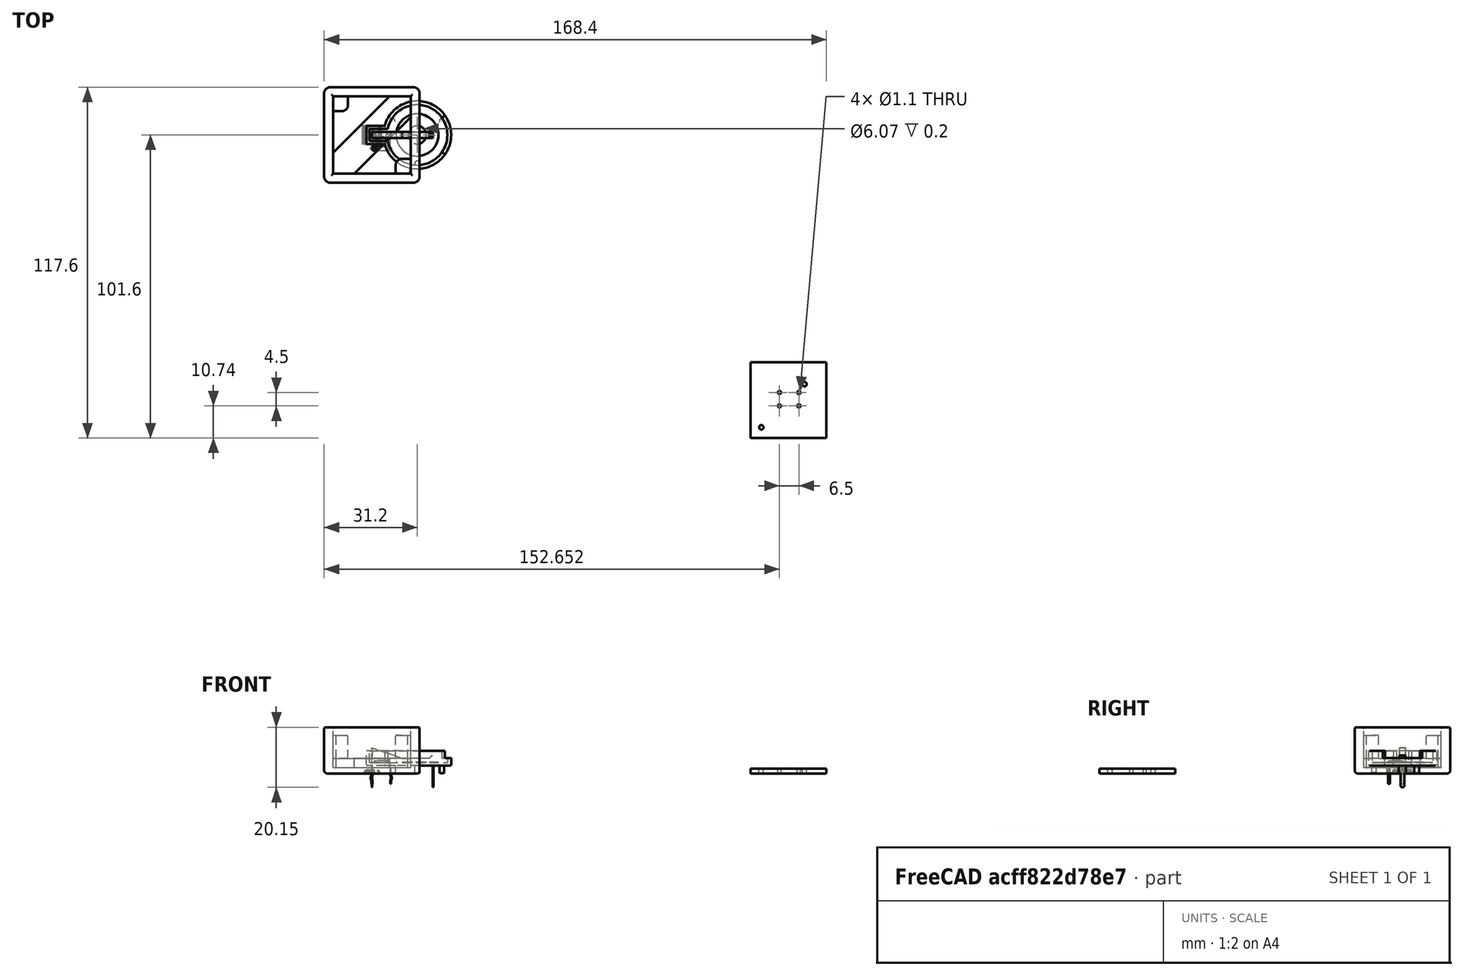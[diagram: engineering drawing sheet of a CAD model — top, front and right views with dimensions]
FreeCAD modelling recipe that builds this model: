
FCSTD DOCUMENT  (FreeCAD 0.18R16131 (Git))
Label: BoxSup
License: All rights reserved
LicenseURL: http://en.wikipedia.org/wiki/All_rights_reserved
objects: Part::Feature×30, App::Part×30, Part::Box×7, Part::Fillet×6, Part::MultiFuse×2, Part::Cut×2
note: 47 computed .brp shape members not serialized (recipe doc carries the construction recipe); baked Part::Feature solids carry a one-line shape summary decoded from their .brp

FEATURE [Part::Box] Box  label="MainInside"
  AttacherType = Attacher::AttachEngine3D
  Height = 20
  Length = 26
  Placement = pos=(-13,-13,-10) rot=(0,0,1;0rad)
  Width = 26
FEATURE [Part::Feature] Part__Feature  label="SOLID"
  shape: bbox 2 x 1.25 x 1.1 mm, 50 faces (baked)
FEATURE [App::Part] LED_0805_2012Metric
  Group = -> [Part__Feature]
  License = CC BY 3.0
  LicenseURL = http://creativecommons.org/licenses/by/3.0/
  Origin = -> Origin
  Placement = pos=(144.272,-79.248,1.65) rot=(0,0,-1;1.5708rad)
FEATURE [Part::Feature] Part__Feature001  label="SOLID001"
  shape: bbox 7.174 x 6 x 7.8 mm, 105 faces (baked)
FEATURE [App::Part] SW_PUSH_6mm
  Group = -> [Part__Feature001]
  License = CC BY 3.0
  LicenseURL = http://creativecommons.org/licenses/by/3.0/
  Origin = -> Origin001
  Placement = pos=(136.652,-86.36,1.65) rot=(0,0,1;0rad)
FEATURE [Part::Feature] Part__Feature002  label="SOLID002"
  shape: bbox 1.6 x 0.8 x 0.45 mm, 26 faces (baked)
FEATURE [App::Part] R_0603_1608Metric
  Group = -> [Part__Feature002]
  License = CC BY 3.0
  LicenseURL = http://creativecommons.org/licenses/by/3.0/
  Origin = -> Origin002
  Placement = pos=(147.701,-98.679,1.65) rot=(0,0,1;0rad)
FEATURE [Part::Feature] Part__Feature003  label="SOLID003"
  shape: bbox 1.6 x 0.8 x 0.45 mm, 26 faces (baked)
FEATURE [App::Part] R_0603_1608Metric001
  Group = -> [Part__Feature003]
  License = CC BY 3.0
  LicenseURL = http://creativecommons.org/licenses/by/3.0/
  Origin = -> Origin003
  Placement = pos=(145.411,-99.187,1.65) rot=(0,0,1;1.5708rad)
FEATURE [Part::Feature] Part__Feature004  label="SOLID004"
  shape: bbox 6.4 x 6.5 x 1.2 mm, 336 faces (baked)
FEATURE [App::Part] TSSOP_20_4_4x6_5mm_P0_65mm
  Group = -> [Part__Feature004]
  License = CC BY 3.0
  LicenseURL = http://creativecommons.org/licenses/by/3.0/
  Origin = -> Origin004
  Placement = pos=(148.336,-93.81,1.65) rot=(0,0,1;1.5708rad)
FEATURE [Part::Feature] Part__Feature005  label="SOLID005"
  shape: bbox 2 x 1.25 x 1.1 mm, 50 faces (baked)
FEATURE [App::Part] LED_0805_2012Metric001
  Group = -> [Part__Feature005]
  License = CC BY 3.0
  LicenseURL = http://creativecommons.org/licenses/by/3.0/
  Origin = -> Origin005
  Placement = pos=(130.556,-79.248,1.65) rot=(0,0,-1;1.5708rad)
FEATURE [Part::Feature] Part__Feature006  label="SOLID006"
  shape: bbox 2 x 1.25 x 1.1 mm, 50 faces (baked)
FEATURE [App::Part] LED_0805_2012Metric002
  Group = -> [Part__Feature006]
  License = CC BY 3.0
  LicenseURL = http://creativecommons.org/licenses/by/3.0/
  Origin = -> Origin006
  Placement = pos=(135.128,-79.248,1.65) rot=(0,0,-1;1.5708rad)
FEATURE [Part::Feature] Part__Feature007  label="SOLID007"
  shape: bbox 2 x 1.25 x 1.1 mm, 50 faces (baked)
FEATURE [App::Part] LED_0805_2012Metric003
  Group = -> [Part__Feature007]
  License = CC BY 3.0
  LicenseURL = http://creativecommons.org/licenses/by/3.0/
  Origin = -> Origin007
  Placement = pos=(139.7,-79.248,1.65) rot=(0,0,-1;1.5708rad)
FEATURE [Part::Feature] Part__Feature008  label="SOLID008"
  shape: bbox 2 x 1.25 x 1.1 mm, 50 faces (baked)
FEATURE [App::Part] LED_0805_2012Metric004
  Group = -> [Part__Feature008]
  License = CC BY 3.0
  LicenseURL = http://creativecommons.org/licenses/by/3.0/
  Origin = -> Origin008
  Placement = pos=(148.844,-79.248,1.65) rot=(0,0,-1;1.5708rad)
FEATURE [Part::Feature] Part__Feature009  label="SOLID009"
  shape: bbox 1.6 x 0.8 x 0.45 mm, 26 faces (baked)
FEATURE [App::Part] R_0603_1608Metric002
  Group = -> [Part__Feature009]
  License = CC BY 3.0
  LicenseURL = http://creativecommons.org/licenses/by/3.0/
  Origin = -> Origin009
  Placement = pos=(132.588,-79.248,1.65) rot=(0,0,-1;1.5708rad)
FEATURE [Part::Feature] Part__Feature010  label="SOLID010"
  shape: bbox 1.6 x 0.8 x 0.45 mm, 26 faces (baked)
FEATURE [App::Part] R_0603_1608Metric003
  Group = -> [Part__Feature010]
  License = CC BY 3.0
  LicenseURL = http://creativecommons.org/licenses/by/3.0/
  Origin = -> Origin010
  Placement = pos=(137.16,-79.248,1.65) rot=(0,0,-1;1.5708rad)
FEATURE [Part::Feature] Part__Feature011  label="SOLID011"
  shape: bbox 1.6 x 0.8 x 0.45 mm, 26 faces (baked)
FEATURE [App::Part] R_0603_1608Metric004
  Group = -> [Part__Feature011]
  License = CC BY 3.0
  LicenseURL = http://creativecommons.org/licenses/by/3.0/
  Origin = -> Origin011
  Placement = pos=(141.732,-79.248,1.65) rot=(0,0,-1;1.5708rad)
FEATURE [Part::Feature] Part__Feature012  label="SOLID012"
  shape: bbox 1.6 x 0.8 x 0.45 mm, 26 faces (baked)
FEATURE [App::Part] R_0603_1608Metric005
  Group = -> [Part__Feature012]
  License = CC BY 3.0
  LicenseURL = http://creativecommons.org/licenses/by/3.0/
  Origin = -> Origin012
  Placement = pos=(146.304,-79.248,1.65) rot=(0,0,-1;1.5708rad)
FEATURE [Part::Feature] Part__Feature013  label="SOLID013"
  shape: bbox 1.6 x 0.8 x 0.45 mm, 26 faces (baked)
FEATURE [App::Part] R_0603_1608Metric006
  Group = -> [Part__Feature013]
  License = CC BY 3.0
  LicenseURL = http://creativecommons.org/licenses/by/3.0/
  Origin = -> Origin013
  Placement = pos=(150.876,-79.248,1.65) rot=(0,0,-1;1.5708rad)
FEATURE [Part::Feature] Part__Feature014  label="SOLID014"
  shape: bbox 1.6 x 0.8 x 0.8 mm, 28 faces (baked)
FEATURE [App::Part] C_0603_1608Metric
  Group = -> [Part__Feature014]
  License = CC BY 3.0
  LicenseURL = http://creativecommons.org/licenses/by/3.0/
  Origin = -> Origin014
  Placement = pos=(142.494,-94.488,1.65) rot=(0,0,-1;1.5708rad)
FEATURE [Part::Feature] Part__Feature015  label="SOLID015"
  shape: bbox 1.6 x 0.8 x 0.8 mm, 28 faces (baked)
FEATURE [App::Part] C_0603_1608Metric001
  Group = -> [Part__Feature015]
  License = CC BY 3.0
  LicenseURL = http://creativecommons.org/licenses/by/3.0/
  Origin = -> Origin015
  Placement = pos=(143.891,-94.488,1.65) rot=(0,0,-1;1.5708rad)
FEATURE [Part::Feature] Part__Feature016  label="SOLID016"
  shape: bbox 1.6 x 0.8 x 0.8 mm, 28 faces (baked)
FEATURE [App::Part] C_0603_1608Metric002
  Group = -> [Part__Feature016]
  License = CC BY 3.0
  LicenseURL = http://creativecommons.org/licenses/by/3.0/
  Origin = -> Origin016
  Placement = pos=(129.286,-95.631,1.65) rot=(0,0,1;0.785398rad)
FEATURE [Part::Feature] Part__Feature017  label="SOLID017"
  shape: bbox 1.6 x 0.8 x 0.8 mm, 28 faces (baked)
FEATURE [App::Part] C_0603_1608Metric003
  Group = -> [Part__Feature017]
  License = CC BY 3.0
  LicenseURL = http://creativecommons.org/licenses/by/3.0/
  Origin = -> Origin017
  Placement = pos=(128.778,-94.107,1.65) rot=(0,0,1;0.785398rad)
FEATURE [Part::Feature] Part__Feature018  label="SOLID018"
  shape: bbox 29.3 x 24.64 x 13.25 mm, 71 faces (baked)
FEATURE [App::Part] BatteryHolder_Keystone_103_1x20mm
  Group = -> [Part__Feature018]
  License = CC BY 3.0
  LicenseURL = http://creativecommons.org/licenses/by/3.0/
  Origin = -> Origin018
  Placement = pos=(130.556,-98.044,-0.05) rot=(0.92388,0.382683,0;3.14159rad)
FEATURE [Part::Feature] Part__Feature019  label="SOLID019"
  shape: bbox 2.5 x 3 x 1.2 mm, 76 faces (baked)
FEATURE [App::Part] SOT_23
  Group = -> [Part__Feature019]
  License = CC BY 3.0
  LicenseURL = http://creativecommons.org/licenses/by/3.0/
  Origin = -> Origin019
  Placement = pos=(130.81,-88.646,1.65) rot=(0,0,1;0rad)
FEATURE [Part::Feature] Part__Feature020  label="SOLID020"
  shape: bbox 2.5 x 3 x 1.2 mm, 76 faces (baked)
FEATURE [App::Part] SOT_23001
  Group = -> [Part__Feature020]
  License = CC BY 3.0
  LicenseURL = http://creativecommons.org/licenses/by/3.0/
  Origin = -> Origin020
  Placement = pos=(129.286,-85.09,1.65) rot=(0,0,1;3.14159rad)
FEATURE [Part::Feature] Part__Feature021  label="SOLID021"
  shape: bbox 1.6 x 0.8 x 0.45 mm, 26 faces (baked)
FEATURE [App::Part] R_0603_1608Metric007
  Group = -> [Part__Feature021]
  License = CC BY 3.0
  LicenseURL = http://creativecommons.org/licenses/by/3.0/
  Origin = -> Origin021
  Placement = pos=(128.27,-88.8745,1.65) rot=(0,0,1;1.5708rad)
FEATURE [Part::Feature] Part__Feature022  label="SOLID022"
  shape: bbox 1.6 x 0.8 x 0.45 mm, 26 faces (baked)
FEATURE [App::Part] R_0603_1608Metric008
  Group = -> [Part__Feature022]
  License = CC BY 3.0
  LicenseURL = http://creativecommons.org/licenses/by/3.0/
  Origin = -> Origin022
  Placement = pos=(131.699,-85.217,1.65) rot=(0,0,1;1.5708rad)
FEATURE [Part::Feature] Part__Feature023  label="SOLID023"
  shape: bbox 2.5 x 3 x 1.2 mm, 76 faces (baked)
FEATURE [App::Part] SOT_23002
  Group = -> [Part__Feature023]
  License = CC BY 3.0
  LicenseURL = http://creativecommons.org/licenses/by/3.0/
  Origin = -> Origin023
  Placement = pos=(135.89,-97.79,1.65) rot=(0,0,1;1.5708rad)
FEATURE [Part::Feature] Part__Feature024  label="SOLID024"
  shape: bbox 2.5 x 3 x 1.2 mm, 76 faces (baked)
FEATURE [App::Part] SOT_23003
  Group = -> [Part__Feature024]
  License = CC BY 3.0
  LicenseURL = http://creativecommons.org/licenses/by/3.0/
  Origin = -> Origin024
  Placement = pos=(139.446,-97.79,1.65) rot=(0,0,1;1.5708rad)
FEATURE [Part::Feature] Part__Feature025  label="SOLID025"
  shape: bbox 2.5 x 3 x 1.2 mm, 76 faces (baked)
FEATURE [App::Part] SOT_23004
  Group = -> [Part__Feature025]
  License = CC BY 3.0
  LicenseURL = http://creativecommons.org/licenses/by/3.0/
  Origin = -> Origin025
  Placement = pos=(143.002,-97.79,1.65) rot=(0,0,1;0rad)
FEATURE [Part::Feature] Part__Feature026  label="SOLID026"
  shape: bbox 1.6 x 0.8 x 0.45 mm, 26 faces (baked)
FEATURE [App::Part] R_0603_1608Metric009
  Group = -> [Part__Feature026]
  License = CC BY 3.0
  LicenseURL = http://creativecommons.org/licenses/by/3.0/
  Origin = -> Origin026
  Placement = pos=(135.89,-100.33,1.65) rot=(0,0,1;3.14159rad)
FEATURE [Part::Feature] Part__Feature027  label="SOLID027"
  shape: bbox 1.6 x 0.8 x 0.45 mm, 26 faces (baked)
FEATURE [App::Part] R_0603_1608Metric010
  Group = -> [Part__Feature027]
  License = CC BY 3.0
  LicenseURL = http://creativecommons.org/licenses/by/3.0/
  Origin = -> Origin027
  Placement = pos=(133.35,-99.5425,1.65) rot=(0,0,-1;1.5708rad)
FEATURE [Part::Feature] Part__Feature028  label="SOLID028"
  shape: bbox 1.6 x 0.8 x 0.45 mm, 26 faces (baked)
FEATURE [App::Part] R_0603_1608Metric011
  Group = -> [Part__Feature028]
  License = CC BY 3.0
  LicenseURL = http://creativecommons.org/licenses/by/3.0/
  Origin = -> Origin028
  Placement = pos=(139.192,-100.33,1.65) rot=(0,0,1;0rad)
FEATURE [Part::Feature] Part__Feature029  label="COMPOUND"
  shape: bbox 25.4 x 25.4 x 1.6 mm, 12 faces (baked)
FEATURE [App::Part] Open_CASCADE_STEP_translator_6_9_1
  Group = -> [LED_0805_2012Metric,SW_PUSH_6mm,R_0603_1608Metric,R_0603_1608Metric001,TSSOP_20_4_4x6_5mm_P0_65mm,LED_0805_2012Metric001,LED_0805_2012Metric002,LED_0805_2012Metric003,LED_0805_2012Metric004,R_0603_1608Metric002,R_0603_1608Metric003,R_0603_1608Metric004,R_0603_1608Metric005,R_0603_1608Metric006,C_0603_1608Metric,C_0603_1608Metric001,C_0603_1608Metric002,C_0603_1608Metric003,+12 more]
  License = CC BY 3.0
  LicenseURL = http://creativecommons.org/licenses/by/3.0/
  Origin = -> Origin029
  Placement = pos=(-139.7,88.9,12.8) rot=(0,0,1;0rad)
FEATURE [Part::Box] Box012  label="KapakGenis"
  AttacherType = Attacher::AttachEngine3D
  Height = 2
  Length = 32
  Placement = pos=(-16,-16,-12) rot=(0,0,1;0rad)
  Width = 32
FEATURE [Part::Box] Box013  label="KapakIc"
  AttacherType = Attacher::AttachEngine3D
  Height = 3
  Length = 26
  Placement = pos=(-13,-13,-10) rot=(0,0,1;0rad)
  Width = 26
FEATURE [Part::Box] Box014  label="KapakCikinti1"
  AttacherType = Attacher::AttachEngine3D
  Height = 7.8
  Length = 5
  Placement = pos=(-13,8,-7) rot=(0,0,1;0rad)
  Width = 5
FEATURE [Part::Box] Box015  label="KapakCikinti2"
  AttacherType = Attacher::AttachEngine3D
  Height = 7.8
  Length = 5
  Placement = pos=(8,-13,-7) rot=(0,0,1;0rad)
  Width = 5
FEATURE [Part::MultiFuse] Fusion001
  Shapes = -> [Box012,Box013,Box014,Box015]
FEATURE [Part::Fillet] Fillet
  Base = -> Fusion001
  Edges = 2 edges r=2: [Edge43,Edge47]
FEATURE [Part::Fillet] Fillet001
  Base = -> Fillet
  Edges = 2 edges r=1: [Edge38,Edge44]
FEATURE [Part::Fillet] Fillet002
  Base = -> Fillet001
  Edges = 6 edges r=2: [Edge5,Edge38,Edge52,Edge53,Edge56,Edge58]
FEATURE [Part::Box] Box001  label="MainOutside"
  AttacherType = Attacher::AttachEngine3D
  Height = 13.5
  Length = 32
  Placement = pos=(-16,-16,-10) rot=(0,0,1;0rad)
  Width = 32
FEATURE [Part::Cut] Cut
  Base = -> Box001
  Tool = -> Box
FEATURE [Part::Fillet] Fillet003
  Base = -> Cut
  Edges = 4 edges r=2: [Edge1,Edge3,Edge6,Edge15]
FEATURE [Part::Box] Box016  label="Cube"
  AttacherType = Attacher::AttachEngine3D
  Height = 10
  Length = 50
  Placement = pos=(-14.1421,-21.2132,-10) rot=(0,0,1;0.785398rad)
  Width = 10
FEATURE [Part::Cut] Cut001
  Base = -> Fillet002
  Tool = -> Box016
FEATURE [Part::MultiFuse] Fusion
  Placement = pos=(0,0,12) rot=(0,0,1;0rad)
  Shapes = -> [Fillet003,Cut001]
FEATURE [Part::Fillet] Fillet004
  Base = -> Fusion
  Edges = 12 edges r=0.5: [Edge1,Edge6,Edge7,Edge8,Edge9,Edge10,Edge11,Edge12,Edge13,Edge14,Edge15,Edge16]
FEATURE [Part::Fillet] Fillet005
  Base = -> Fillet004
  Edges = 8 edges r=1: [Edge14,Edge20,Edge37,Edge39,Edge40,Edge41,Edge42,Edge43]
